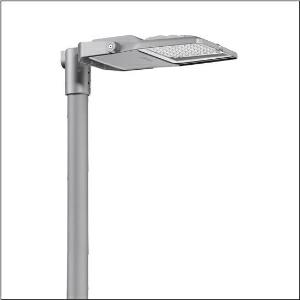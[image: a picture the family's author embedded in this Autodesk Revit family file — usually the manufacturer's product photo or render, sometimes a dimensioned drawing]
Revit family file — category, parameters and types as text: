
# Revit family: floodlight_fl_21_iq_mini___pl33t_5xa7772c2f3a_076b
name_source: partatom
category: Lighting Fixtures
units: mm (PartAtom-declared; Revit-internal decimal feet)

## family parameters
Cut with Voids When Loaded = No
Host = Face
Light Source = No
Part Type = Normal
Room Calculation Point = No
Round Connector Dimension = Use Diameter
Shared = No

## types (1)
- --- (1 x LED, 12060 lm, 87.2 W, 3000K)
    Apparent Load = 87 VA
    CIE Flux Codes = 26 75 99 100 100
    Color Rendering = 70
    Color Temperature = 3000K
    Default Elevation = 1800 mm
    Description = Floodlight FL 21 iQ mini, floodlight, primary light control with lens, of PMMA, primary optical cover: protective disc, of toughened safety glass, transparent, light distribution: PL33T, light emission: direct distribution, installation type: surface-mounted, LED, High Power LED, rated luminous flux: 12.060lm, luminous efficacy: 138lm/W, light colour: 730, colour temperature: 3000K, control: Auto-Match, Temp-Guard, Night-Set, Smart-Wire, Desk-Remote (wireless, voltage-free reading and setting of iQ features in the workshop via application-optimized NFC function/RFID function), optimised constant luminous flux control (CLO 2.0), Light-Fading, Lumen-Switch, with terminal, 6-pole, mains connection: 220..240V, AC, 50/60Hz, start of lifetime: 87W, end of service life: 92W, reduction: 40W, luminaire housing, of diecast aluminium, powder-coated, Siteco® metallic grey (DB 702S), corrosivity category C5 mid according to DIN EN ISO 12944, sealing non-destructively replaceable, please order mast flange separately, mast bracket, of steel, galvanised, powder-coated, protection rating (complete): IP66, insulation class (complete): insulation class II (safety insulation), certification: CE, ENEC, VDE, protection symbol: D, impact resistance: IK08, permissible operating ambient temperature: -40..+40°C, permissible operating ambient temperature for outdoor applications: -40..+50°C, standard: DIN EN 12944, LABS conformity tested according to VDMA 24364:2018-05, packaging unit: 1 piece

Light Distribution: PL33T
    Height = 70 mm
    Lamp = 1 x LED
    Lamp Light Flux = 12060 lm
    Lamp Power = 87.2 W
    Lamp count = 1
    Length = 485 mm
    Luminous efficacy = 138 lm/W
    Manufacturer = Siteco
    ModVariant = No
    Model = 5XA7772C2F3A
    Number of Poles = 1
    OnlyDefault = Yes
    Power Factor = 1
    Product Name = Floodlight FL 21 iQ mini | PL33T
    Product group = floodlight | pylon annexe
    ProductGroupID = 6200
    Protection Class = Protection class II
    Protection Degree = IP 66
    RLX_Detail_Level = 1
    RLX_Emergency_Light_Flux = 0 lm
    RLX_Emergency_Type = 0
    RLX_Emergency_Type_DB = No
    RlxData = <blob elided: 101257 chars, md5=90f436d4>
    Socket = socket
    Standby Power = 0 W
    System Light Flux = 12060 lm
    System Power = 87 W
    Type Comments = factory setting: luminous flux: 100 % | dim-lin: 254 | 456 mA
    Type Image = l_1007125.jpg
    URL = http://relux.com
    VarID = @adj_119825
    Voltage = 0 V
    Weight = 0.00 kg
    Width = 337 mm

## geometry (parser evidence)
native form markers: Blend x4, Sweep x10
no freeform markers — native parametric forms only
